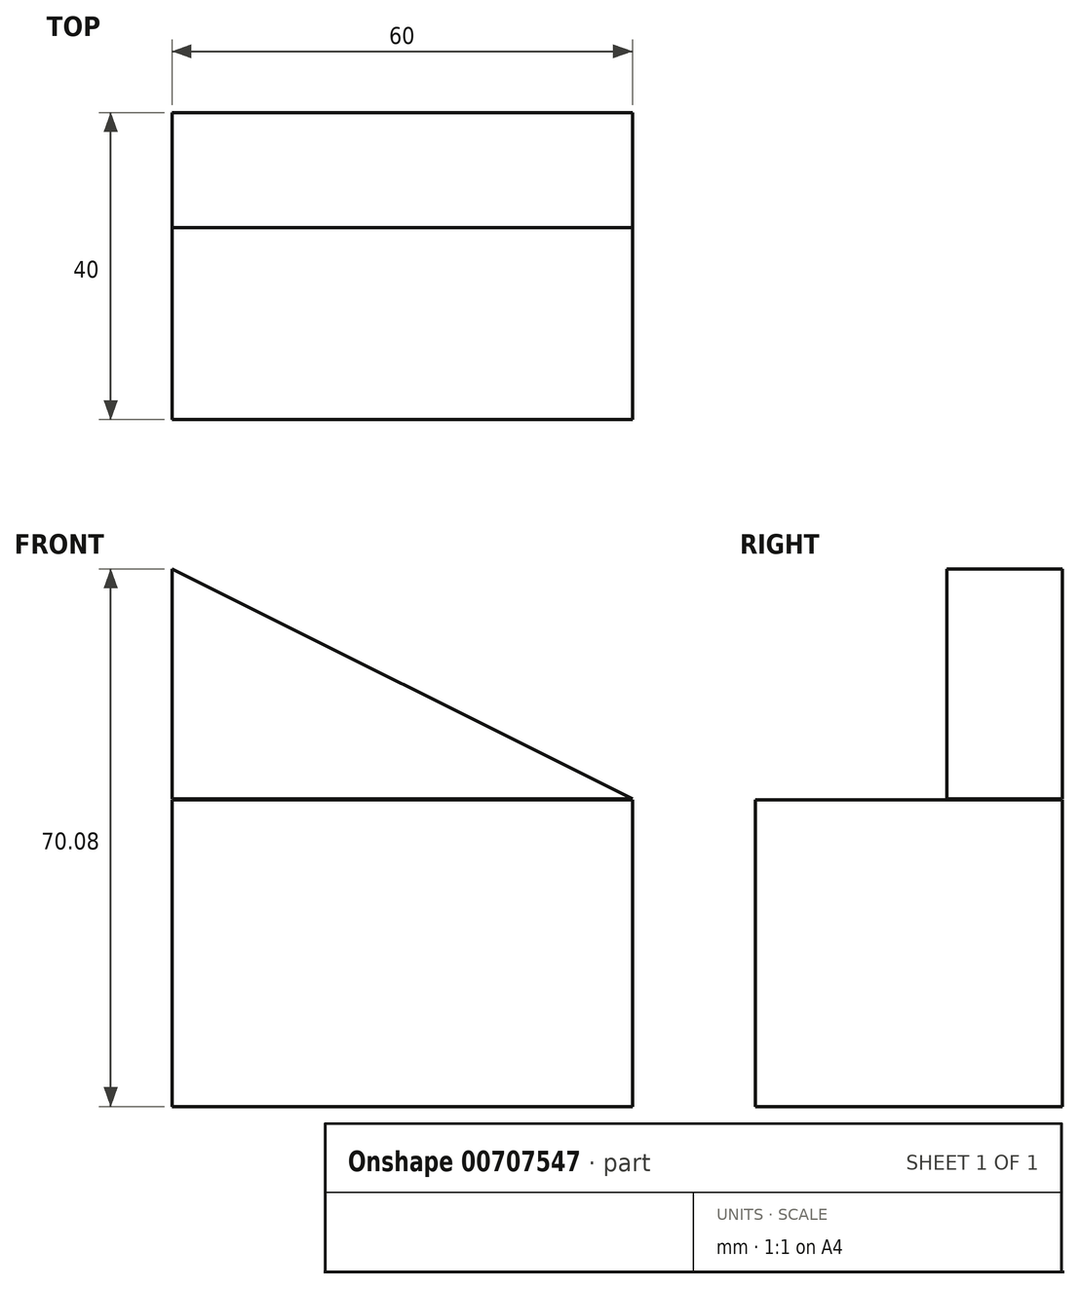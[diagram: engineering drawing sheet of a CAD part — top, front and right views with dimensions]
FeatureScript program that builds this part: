
annotation { "Feature Type Name" : "Feature", "Feature Type Description" : "" }
export const myFeature = defineFeature(function(context is Context, id is Id, definition is map)
    precondition{}
    {
        {
            var Q0;
            Q0=qCreatedBy(makeId("Front.planeOp"),FACE);
            var sketch = newSketch(context, id + "F0", { "sketchPlane" : qUnion([Q0])});
            skLineSegment(sketch, "E0.bottom", {"start": v(0, 0) * mm, "end": v(60, 0) * mm});
            skLineSegment(sketch, "E0.top", {"start": v(0, 40) * mm, "end": v(60, 40) * mm});
            skLineSegment(sketch, "E0.left", {"start": v(0, 0) * mm, "end": v(0, 40) * mm});
            skLineSegment(sketch, "E0.right", {"start": v(60, 0) * mm, "end": v(60, 40) * mm});
            skSolve(sketch);
        }
        {
            var Q0;
            Q0 = qSketchRegion(id + "F0", true);
            extrude(context, id + "F1", {"entities" : qUnion([Q0]), "depth" : 40 * mm, "offsetDistance" : 25 * mm});
        }
        {
            var Q0;
            Q0=makeQuery(id+"F1.opExtrude","SWEPT_FACE",FACE,{"disambiguationData":[OSD([sQuery(id+"F0.wireOp",EDGE,"E0.top")])]});
            var sketch = newSketch(context, id + "F2", { "sketchPlane" : qUnion([Q0])});
            skLineSegment(sketch, "E1", {"start": v(20, 0) * mm, "end": v(20, -25) * mm});
            skLineSegment(sketch, "E2", {"start": v(0, 0) * mm, "end": v(20, 0) * mm});
            skCircle(sketch, "E3", {"center": v(20, -25) * mm, "radius": 7.5 * mm});
            skSolve(sketch);
        }
        {
            var Q0;
            Q0=qCreatedBy(makeId("Front.planeOp"),FACE);
            var sketch = newSketch(context, id + "F3", { "sketchPlane" : qUnion([Q0])});
            skLineSegment(sketch, "E4", {"start": v(0, 40.08) * mm, "end": v(0, 70.08) * mm});
            skLineSegment(sketch, "E5", {"start": v(0, 40.08) * mm, "end": v(60, 40.08) * mm});
            skLineSegment(sketch, "E6", {"start": v(60, 40.08) * mm, "end": v(0, 70.08) * mm});
            skSolve(sketch);
        }
        {
            var Q0;
            Q0 = qSketchRegion(id + "F3", true);
            extrude(context, id + "F4", {"entities" : qUnion([Q0]), "depth" : 15 * mm, "offsetDistance" : 25 * mm});
        }
    });
